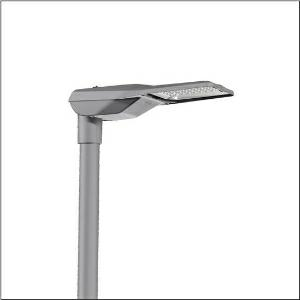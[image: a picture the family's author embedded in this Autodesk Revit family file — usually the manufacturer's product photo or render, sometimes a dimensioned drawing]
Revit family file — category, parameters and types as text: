
# Revit family: streetlight_sl_21_mini___st1_5a_5xe2p33s08hb_d0bc
name_source: partatom
category: Lighting Fixtures
units: mm (PartAtom-declared; Revit-internal decimal feet)

## family parameters
Cut with Voids When Loaded = No
Host = Face
Light Source = No
Part Type = Normal
Room Calculation Point = No
Round Connector Dimension = Use Diameter
Shared = No

## types (1)
- --- (1 x LED, 8890 lm, 66 W, 3000K)
    Apparent Load = 66 VA
    CIE Flux Codes = 22 53 95 100 100
    Color Rendering = 70
    Color Temperature = 3000K
    Default Elevation = 1800 mm
    Description = Streetlight SL 21 mini, mast luminaire, primary light control with lens, of PMMA, primary optical cover: cover, of toughened safety glass, transparent, light distribution: ST1.5a, light emission: direct distribution, primary light characteristic: asymmetric, installation type: side-entry, post-top, LED, High Power LED, rated luminous flux: 8.890lm, luminous efficacy: 135lm/W, light colour: 730, colour temperature: 3000K, control gear: D4i, control: overheat protection, constant luminous flux control, time-dependent luminous flux control, flexible luminous flux parameterisation, pre-setting: logarithmic dimming characteristic, mains connection: 220..240V, AC, 50/60Hz, start of lifetime: 66W, end of service life: 69W, reduction: 30W, luminaire housing, of diecast aluminium, powder-coated, SITECO metallic grey (DB 702S), corrosivity category C5 high according to DIN EN ISO 12944, please order mast flange separately, inclination adjustable: 0°, 5°, 10°, 15°, sealing non-destructively replaceable, multi-level sealing system, length: 628mm, width: 235mm, height: 110mm, mast flange for spigot size: 42mm (side-entry): 5XC10008XM4, 60/48mm (side-entry/post-top): 5XC10108XM2, 76/60mm (side-entry/post-top): 5XC10108XM1, mounting height: 4..8m, Smart Interface above, protection rating (complete): IP66, insulation class (complete): insulation class II (safety insulation), certification: CE, ENEC, ENEC+, VDE, impact resistance: IK10, permissible operating ambient temperature for outdoor applications: -40..+50°C, standard-compliant lighting for roads and squares, packaging unit: 1 piece

Light Distribution: ST1.5a
    Height = 110 mm
    Lamp = 1 x LED
    Lamp Light Flux = 8890 lm
    Lamp Power = 66 W
    Lamp count = 1
    Length = 625 mm
    Luminous efficacy = 135 lm/W
    Manufacturer = Siteco
    ModVariant = No
    Model = 5XE2P33S08HB
    Number of Poles = 1
    OnlyDefault = Yes
    Power Factor = 1
    Product Name = Streetlight SL 21 mini | ST1.5a
    Product group = mast luminaire | pylon top
    ProductGroupID = 6100
    Protection Class = Protection class II
    Protection Degree = IP 66
    RLX_Detail_Level = 1
    RLX_Emergency_Light_Flux = 0 lm
    RLX_Emergency_Type = 0
    RLX_Emergency_Type_DB = No
    RlxData = <blob elided: 29545 chars, md5=a90dd2bc>
    Socket = socket
    Standby Power = 0 W
    System Light Flux = 8890 lm
    System Power = 66 W
    Type Comments = factory setting: luminous flux: 100 % | dim-lin: 254 | 670 mA
    Type Image = l_1003515.jpg
    URL = http://relux.com
    VarID = @adj_175125
    Voltage = 0 V
    Weight = 0.00 kg
    Width = 234 mm

## geometry (parser evidence)
native form markers: Blend x4, Sweep x10
no freeform markers — native parametric forms only
